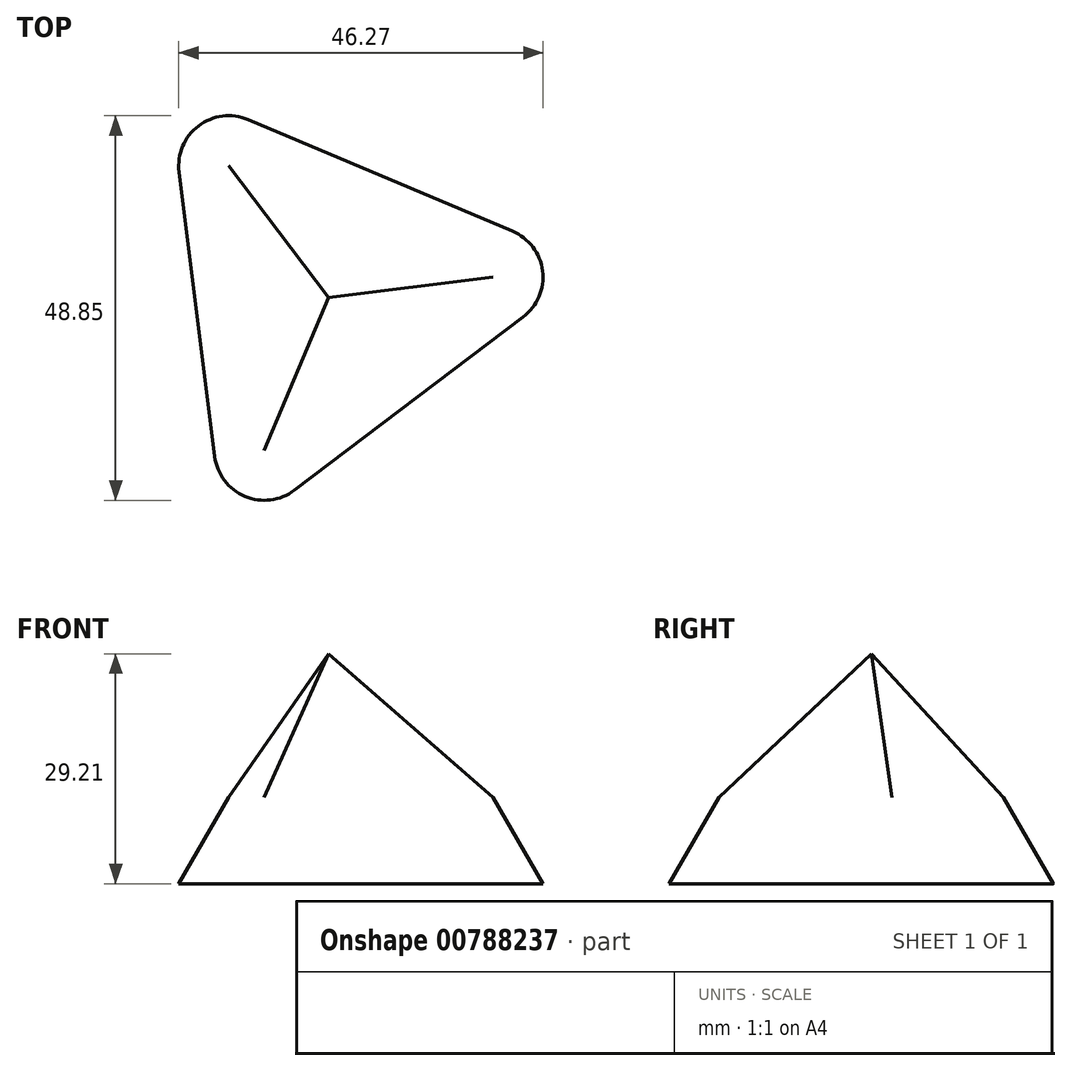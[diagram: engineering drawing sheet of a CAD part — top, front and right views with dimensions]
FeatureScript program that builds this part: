
annotation { "Feature Type Name" : "Feature", "Feature Type Description" : "" }
export const myFeature = defineFeature(function(context is Context, id is Id, definition is map)
    precondition{}
    {
        {
            var Q0;
            Q0=qCreatedBy(makeId("Top.planeOp"),FACE);
            var sketch = newSketch(context, id + "F0", { "sketchPlane" : qUnion([Q0])});
            skCircle(sketch, "E0.cCircle", {"center": v(-28.91, 24.2) * mm, "radius": 16.87 * mm, "construction": true});
            skLineSegment(sketch, "E0.0", {"start": v(-4.2, 21.75) * mm, "end": v(-33.25, -0.24) * mm});
            skLineSegment(sketch, "E0.1", {"start": v(-43.39, 4.04) * mm, "end": v(-47.9, 40.19) * mm});
            skLineSegment(sketch, "E0.2", {"start": v(-39.14, 46.82) * mm, "end": v(-5.57, 32.67) * mm});
            skPoint(sketch, "E0.0.midPoint", {"position": v(-18.73, 10.76) * mm});
            skPoint(sketch, "E1.visualSharp", {"position": v(-49.27, 51.1) * mm});
            skArc(sketch, "E1.filletArc", {"start": v(-39.14, 46.82) * mm, "mid": v(-45.44, 46.04) * mm, "end": v(-47.9, 40.19) * mm});
            skPoint(sketch, "E2.visualSharp", {"position": v(4.56, 28.4) * mm});
            skArc(sketch, "E2.filletArc", {"start": v(-4.2, 21.75) * mm, "mid": v(-1.74, 27.6) * mm, "end": v(-5.57, 32.67) * mm});
            skPoint(sketch, "E3.visualSharp", {"position": v(-42.02, -6.88) * mm});
            skArc(sketch, "E3.filletArc", {"start": v(-43.39, 4.04) * mm, "mid": v(-39.55, -1.03) * mm, "end": v(-33.25, -0.24) * mm});
            skSolve(sketch);
        }
        {
            var Q0;
            Q0=makeQuery(id+"F0.imprint","IMPRINT",FACE,{"disambiguationData":[TD([[makeQuery(id+"F0.imprint","IMPRINT",EDGE,{"derivedFrom":sQuery(id+"F0.wireOp",EDGE,"E0.0")}),-1.0]])]});
            extrude(context, id + "F1", {"entities" : qUnion([Q0]), "depth" : 32 * mm, "offsetDistance" : 25.4 * mm, "hasDraft" : true, "draftAngle" : 30 * degree, "draftPullDirection" : true});
        }
    });
